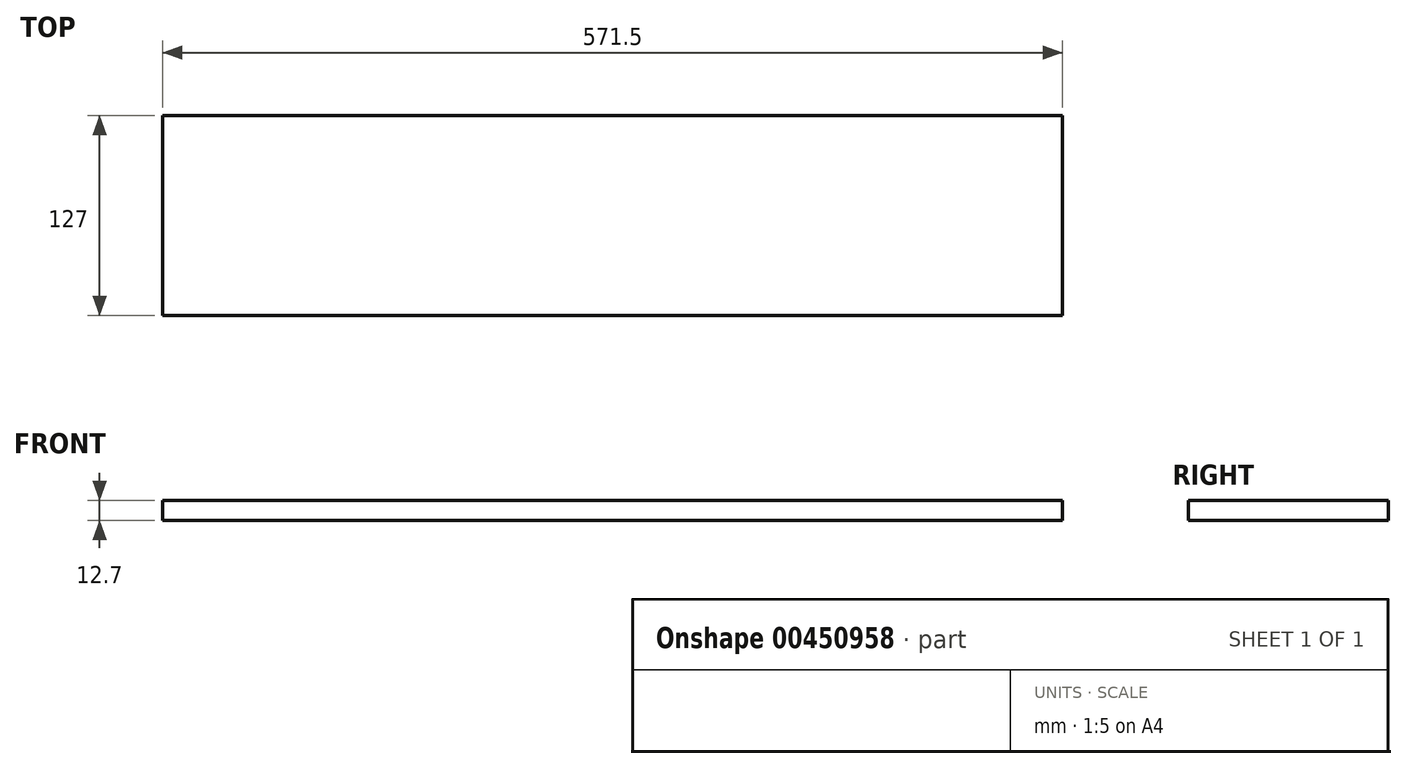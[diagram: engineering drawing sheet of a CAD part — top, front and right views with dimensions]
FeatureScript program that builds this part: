
annotation { "Feature Type Name" : "Feature", "Feature Type Description" : "" }
export const myFeature = defineFeature(function(context is Context, id is Id, definition is map)
    precondition{}
    {
        {
            var Q0;
            Q0=qCreatedBy(makeId("Top.planeOp"),FACE);
            var sketch = newSketch(context, id + "F0", { "sketchPlane" : qUnion([Q0])});
            skLineSegment(sketch, "E0.bottom", {"start": v(-285.75, 63.5) * mm, "end": v(285.75, 63.5) * mm});
            skLineSegment(sketch, "E0.top", {"start": v(-285.75, -63.5) * mm, "end": v(285.75, -63.5) * mm});
            skLineSegment(sketch, "E0.left", {"start": v(-285.75, 63.5) * mm, "end": v(-285.75, -63.5) * mm});
            skLineSegment(sketch, "E0.right", {"start": v(285.75, 63.5) * mm, "end": v(285.75, -63.5) * mm});
            skSolve(sketch);
        }
        {
            var Q0;
            Q0 = qSketchRegion(id + "F0", true);
            extrude(context, id + "F1", {"entities" : qUnion([Q0]), "depth" : 12.7 * mm});
        }
    });
